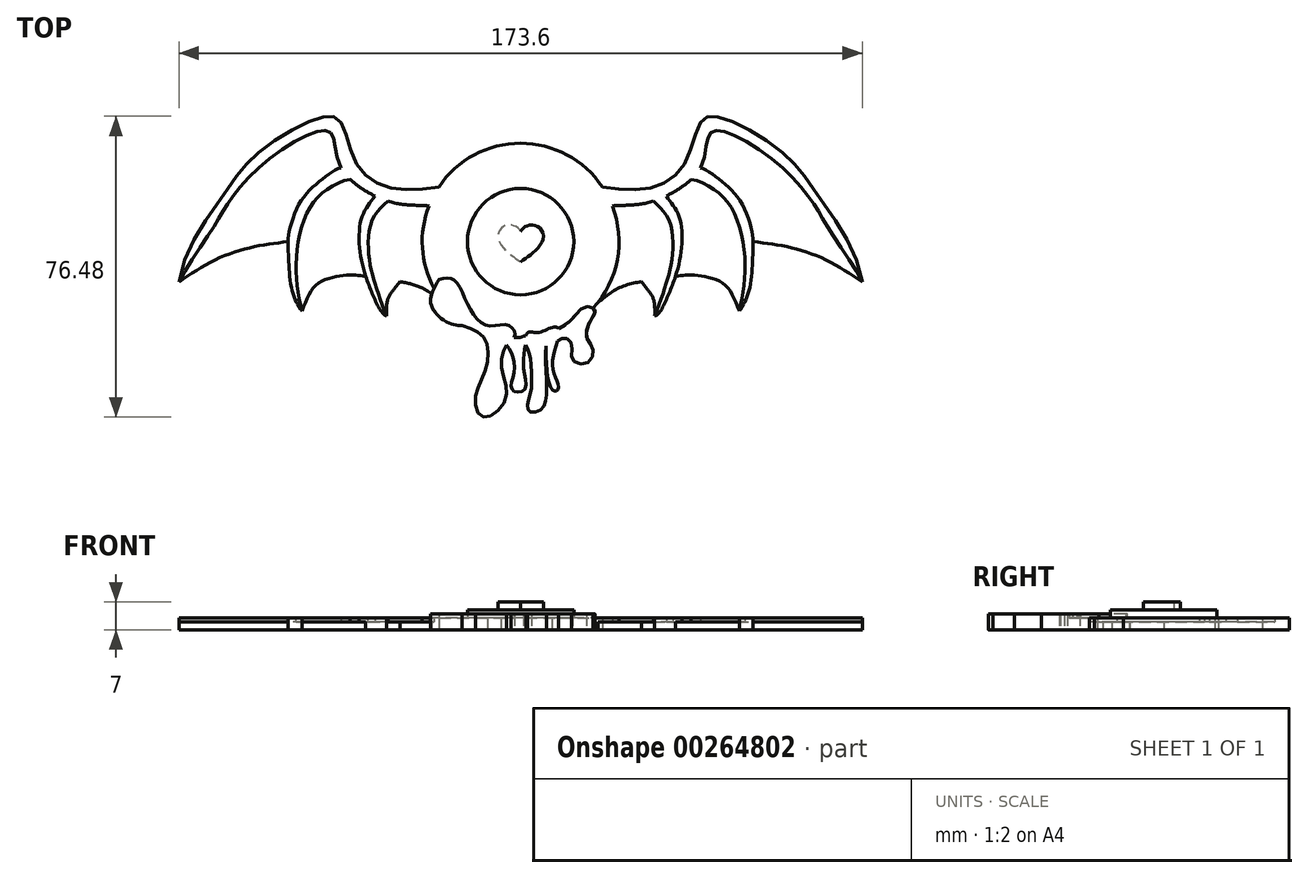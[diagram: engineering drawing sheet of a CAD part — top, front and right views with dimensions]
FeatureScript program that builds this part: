
annotation { "Feature Type Name" : "Feature", "Feature Type Description" : "" }
export const myFeature = defineFeature(function(context is Context, id is Id, definition is map)
    precondition{}
    {
        {
            var Q0;
            Q0=qCreatedBy(makeId("Top.planeOp"),FACE);
            var sketch = newSketch(context, id + "F0", { "sketchPlane" : qUnion([Q0])});
            skCircle(sketch, "E0", {"center": v(0, 0) * mm, "radius": 25 * mm});
            skLineSegment(sketch, "E1", {"start": v(0, 25) * mm, "end": v(0, -25) * mm, "construction": true});
            skFitSpline(sketch, "E2", {"points": [v(20.76, 13.92) * mm, v(34.08, 13.92) * mm, v(42, 20.48) * mm, v(46, 30.69) * mm, v(50.93, 31.48) * mm, v(67.03, 22.24) * mm, v(75.74, 11.46) * mm, v(86.8, -10.28) * mm], "startDerivative": vector(95.75, -17.53) * mm, "endDerivative": vector(18.54, -135.11) * mm});
            skFitSpline(sketch, "E3", {"points": [v(20.7, -14) * mm, v(37, -10.54) * mm, v(45, -8.07) * mm, v(66.66, 1.74) * mm, v(75.74, 11.46) * mm], "startDerivative": vector(59.46, -0.59) * mm, "endDerivative": vector(18.77, 28.66) * mm, "construction": true});
            skFitSpline(sketch, "E4", {"points": [v(23.3, 9.08) * mm, v(33.72, 10.28) * mm, v(45.64, 18.76) * mm, v(47.9, 27.18) * mm, v(51.1, 28.14) * mm, v(65.44, 19.69) * mm, v(74.45, 9.58) * mm, v(78.2, 3.43) * mm, v(86.8, -10.28) * mm], "startDerivative": vector(110.38, 5.87) * mm, "endDerivative": vector(40.39, -81.17) * mm});
            skFitSpline(sketch, "E5", {"points": [v(33.72, 10.28) * mm, v(37.86, 5.02) * mm, v(38.5, -3.9) * mm, v(37, -10.54) * mm, v(34.08, -18.9) * mm], "startDerivative": vector(21.3, -19.5) * mm, "endDerivative": vector(-13.55, -34.2) * mm});
            skFitSpline(sketch, "E6", {"points": [v(37, 11.6) * mm, v(40.25, 6.46) * mm, v(40.52, -4.24) * mm, v(37.2, -14.33) * mm, v(34.08, -18.9) * mm], "startDerivative": vector(14.85, -22) * mm, "endDerivative": vector(-16.96, -5.17) * mm});
            skFitSpline(sketch, "E7", {"points": [v(32.11, -12.01) * mm, v(33.72, -14.49) * mm, v(34.08, -18.9) * mm], "startDerivative": vector(4.43, -5.79) * mm, "endDerivative": vector(-0.15, -8.8) * mm});
            skFitSpline(sketch, "E8", {"points": [v(45.64, 18.76) * mm, v(50.26, 15.97) * mm, v(55.72, 10.44) * mm, v(58.9, 2) * mm, v(59.02, -2.64) * mm, v(58.1, -12.2) * mm, v(55.56, -17.62) * mm], "startDerivative": vector(28.21, -5.42) * mm, "endDerivative": vector(-19.1, -30.2) * mm});
            skFitSpline(sketch, "E9", {"points": [v(43.34, 15.84) * mm, v(49.55, 13.02) * mm, v(53.96, 7.9) * mm, v(56.67, -1.36) * mm, v(56.83, -10.28) * mm, v(55.56, -17.62) * mm], "startDerivative": vector(32.47, -4.35) * mm, "endDerivative": vector(-7.91, -36.84) * mm});
            skFitSpline(sketch, "E10", {"points": [v(38.97, -9.94) * mm, v(46.63, -10.28) * mm, v(52.84, -13.22) * mm, v(55.56, -17.62) * mm], "startDerivative": vector(21.38, 0.7) * mm, "endDerivative": vector(7.12, -15.9) * mm, "construction": true});
            skFitSpline(sketch, "E11", {"points": [v(59.1, 0) * mm, v(68, -1.36) * mm, v(77.72, -4.7) * mm, v(86.8, -10.28) * mm], "startDerivative": vector(27.78, -3.23) * mm, "endDerivative": vector(25.67, -17.5) * mm});
            skFitSpline(sketch, "E12", {"points": [v(19.62, -15.5) * mm, v(25.1, -11.72) * mm, v(30.69, -10.12) * mm], "startDerivative": vector(10.4, 8.3) * mm, "endDerivative": vector(11.78, 2.35) * mm});
            skFitSpline(sketch, "E13", {"points": [v(32.11, -12.01) * mm, v(30.69, -10.12) * mm], "startDerivative": vector(-1.42, 1.9) * mm, "endDerivative": vector(-1.42, 1.9) * mm});
            skFitSpline(sketch, "E14", {"points": [v(55.56, -17.62) * mm, v(52.05, -11.08) * mm, v(46.6, -8.83) * mm, v(42.13, -8.5) * mm, v(39.36, -8.79) * mm], "startDerivative": vector(-10.96, 25.87) * mm, "endDerivative": vector(-14.04, -2.02) * mm});
            skFitSpline(sketch, "E15", {"points": [v(20.76, 13.92) * mm, v(16.18, 9.49) * mm, v(19.62, -15.5) * mm], "startDerivative": vector(-16.85, -9.2) * mm, "endDerivative": vector(11.44, -45.62) * mm});
            skFitSpline(sketch, "E16.MirrorCS", {"points": [v(-20.76, 13.92) * mm, v(-16.18, 9.49) * mm, v(-19.62, -15.5) * mm], "startDerivative": vector(16.85, -9.2) * mm, "endDerivative": vector(-11.44, -45.62) * mm});
            skFitSpline(sketch, "E17.MirrorCS", {"points": [v(-23.3, 9.08) * mm, v(-33.72, 10.28) * mm, v(-45.64, 18.76) * mm, v(-47.9, 27.18) * mm, v(-51.1, 28.14) * mm, v(-65.44, 19.69) * mm, v(-74.45, 9.58) * mm, v(-78.2, 3.43) * mm, v(-86.8, -10.28) * mm], "startDerivative": vector(-110.38, 5.87) * mm, "endDerivative": vector(-40.39, -81.17) * mm});
            skFitSpline(sketch, "E18.MirrorCS", {"points": [v(-20.76, 13.92) * mm, v(-34.08, 13.92) * mm, v(-42, 20.48) * mm, v(-46, 30.69) * mm, v(-50.93, 31.48) * mm, v(-67.03, 22.24) * mm, v(-75.74, 11.46) * mm, v(-86.8, -10.28) * mm], "startDerivative": vector(-95.75, -17.53) * mm, "endDerivative": vector(-18.54, -135.11) * mm});
            skFitSpline(sketch, "E19.MirrorCS", {"points": [v(-33.72, 10.28) * mm, v(-37.86, 5.02) * mm, v(-38.5, -3.9) * mm, v(-37, -10.54) * mm, v(-34.08, -18.9) * mm], "startDerivative": vector(-21.3, -19.5) * mm, "endDerivative": vector(13.55, -34.2) * mm});
            skFitSpline(sketch, "E20.MirrorCS", {"points": [v(-37, 11.6) * mm, v(-40.25, 6.46) * mm, v(-40.52, -4.24) * mm, v(-37.2, -14.33) * mm, v(-34.08, -18.9) * mm], "startDerivative": vector(-14.85, -22) * mm, "endDerivative": vector(16.96, -5.17) * mm});
            skFitSpline(sketch, "E21.MirrorCS", {"points": [v(-43.34, 15.84) * mm, v(-49.55, 13.02) * mm, v(-53.96, 7.9) * mm, v(-56.67, -1.36) * mm, v(-56.83, -10.28) * mm, v(-55.56, -17.62) * mm], "startDerivative": vector(-32.47, -4.35) * mm, "endDerivative": vector(7.91, -36.84) * mm});
            skFitSpline(sketch, "E22.MirrorCS", {"points": [v(-45.64, 18.76) * mm, v(-50.26, 15.97) * mm, v(-55.72, 10.44) * mm, v(-58.9, 2) * mm, v(-59.02, -2.64) * mm, v(-58.1, -12.2) * mm, v(-55.56, -17.62) * mm], "startDerivative": vector(-28.21, -5.42) * mm, "endDerivative": vector(19.1, -30.2) * mm});
            skFitSpline(sketch, "E23.MirrorCS", {"points": [v(-19.62, -15.5) * mm, v(-25.1, -11.72) * mm, v(-30.69, -10.12) * mm], "startDerivative": vector(-10.4, 8.3) * mm, "endDerivative": vector(-11.78, 2.35) * mm});
            skFitSpline(sketch, "E24.MirrorCS", {"points": [v(-32.11, -12.01) * mm, v(-30.69, -10.12) * mm], "startDerivative": vector(1.42, 1.9) * mm, "endDerivative": vector(1.42, 1.9) * mm});
            skFitSpline(sketch, "E25.MirrorCS", {"points": [v(-32.11, -12.01) * mm, v(-33.72, -14.49) * mm, v(-34.08, -18.9) * mm], "startDerivative": vector(-4.43, -5.79) * mm, "endDerivative": vector(0.15, -8.8) * mm});
            skFitSpline(sketch, "E26.MirrorCS", {"points": [v(-59.1, 0) * mm, v(-68, -1.36) * mm, v(-77.72, -4.7) * mm, v(-86.8, -10.28) * mm], "startDerivative": vector(-27.78, -3.23) * mm, "endDerivative": vector(-25.67, -17.5) * mm});
            skFitSpline(sketch, "E27.MirrorCS", {"points": [v(-55.56, -17.62) * mm, v(-52.05, -11.08) * mm, v(-46.6, -8.83) * mm, v(-42.13, -8.5) * mm, v(-39.36, -8.79) * mm], "startDerivative": vector(10.96, 25.87) * mm, "endDerivative": vector(14.04, -2.02) * mm});
            skSolve(sketch);
        }
        {
            var Q0;
            {var subQ0=sQuery(id+"F0.wireOp",EDGE,"E15");Q0=makeQuery(id+"F0.imprint","IMPRINT",FACE,{"disambiguationData":[TD([[makeQuery(id+"F0.imprint","IMPRINT",EDGE,{"derivedFrom":subQ0}),-1.0]])]});}
            var Q1;
            {var subQ0=sQuery(id+"F0.wireOp",EDGE,"E15");Q1=makeQuery(id+"F0.imprint","IMPRINT",FACE,{"disambiguationData":[TD([[makeQuery(id+"F0.imprint","IMPRINT",EDGE,{"derivedFrom":subQ0}),1.0]])]});}
            var Q2;
            {var subQ0=sQuery(id+"F0.wireOp",EDGE,"E16.MirrorCS");Q2=makeQuery(id+"F0.imprint","IMPRINT",FACE,{"disambiguationData":[TD([[makeQuery(id+"F0.imprint","IMPRINT",EDGE,{"derivedFrom":subQ0}),-1.0]])]});}
            extrude(context, id + "F1", {"entities" : qUnion([Q0, Q1, Q2]), "depth" : 3 * mm, "offsetDistance" : 25 * mm});
        }
        {
            var Q0;
            Q0=qCreatedBy(makeId("Top.planeOp"),FACE);
            var sketch = newSketch(context, id + "F2", { "sketchPlane" : qUnion([Q0])});
            skCircle(sketch, "E28", {"center": v(0, 0) * mm, "radius": 13.5 * mm});
            skSolve(sketch);
        }
        {
            var Q0;
            Q0=qSketchRegion(id+"F2",true);
            extrude(context, id + "F3", {"entities" : qUnion([Q0]), "operationType" : NewBodyOperationType.ADD, "depth" : 5 * mm, "offsetDistance" : 25 * mm});
        }
        {
            var Q0;
            {var subQ4=sQuery(id+"F0.wireOp",EDGE,"E2");Q0=makeQuery(id+"F0.imprint","IMPRINT",FACE,{"disambiguationData":[TD([[makeQuery(id+"F0.imprint","IMPRINT",EDGE,{"derivedFrom":subQ4}),-1.0]])]});}
            var Q1;
            {var subQ0=sQuery(id+"F0.wireOp",EDGE,"E15");Q1=makeQuery(id+"F0.imprint","IMPRINT",FACE,{"disambiguationData":[TD([[makeQuery(id+"F0.imprint","IMPRINT",EDGE,{"derivedFrom":subQ0}),1.0]])]});}
            var Q2;
            {var subQ0=sQuery(id+"F0.wireOp",EDGE,"E5");Q2=makeQuery(id+"F0.imprint","IMPRINT",FACE,{"disambiguationData":[TD([[makeQuery(id+"F0.imprint","IMPRINT",EDGE,{"derivedFrom":subQ0}),-1.0]])]});}
            var Q3;
            {var subQ0=sQuery(id+"F0.wireOp",EDGE,"E5");Q3=makeQuery(id+"F0.imprint","IMPRINT",FACE,{"disambiguationData":[TD([[makeQuery(id+"F0.imprint","IMPRINT",EDGE,{"derivedFrom":subQ0}),1.0]])]});}
            var Q4;
            {var subQ3=sQuery(id+"F0.wireOp",EDGE,"E9");Q4=makeQuery(id+"F0.imprint","IMPRINT",FACE,{"disambiguationData":[TD([[makeQuery(id+"F0.imprint","IMPRINT",EDGE,{"derivedFrom":subQ3}),-1.0]])]});}
            var Q5;
            {var subQ3=sQuery(id+"F0.wireOp",EDGE,"E9");Q5=makeQuery(id+"F0.imprint","IMPRINT",FACE,{"disambiguationData":[TD([[makeQuery(id+"F0.imprint","IMPRINT",EDGE,{"derivedFrom":subQ3}),1.0]])]});}
            var Q6;
            {var subQ0=sQuery(id+"F0.wireOp",EDGE,"E11");Q6=makeQuery(id+"F0.imprint","IMPRINT",FACE,{"disambiguationData":[TD([[makeQuery(id+"F0.imprint","IMPRINT",EDGE,{"derivedFrom":subQ0}),1.0]])]});}
            var Q7;
            {var subQ1=sQuery(id+"F0.wireOp",EDGE,"E19.MirrorCS");Q7=makeQuery(id+"F0.imprint","IMPRINT",FACE,{"disambiguationData":[TD([[makeQuery(id+"F0.imprint","IMPRINT",EDGE,{"derivedFrom":subQ1}),1.0]])]});}
            var Q8;
            {var subQ3=sQuery(id+"F0.wireOp",EDGE,"E21.MirrorCS");Q8=makeQuery(id+"F0.imprint","IMPRINT",FACE,{"disambiguationData":[TD([[makeQuery(id+"F0.imprint","IMPRINT",EDGE,{"derivedFrom":subQ3}),1.0]])]});}
            var Q9;
            {var subQ0=sQuery(id+"F0.wireOp",EDGE,"E19.MirrorCS");Q9=makeQuery(id+"F0.imprint","IMPRINT",FACE,{"disambiguationData":[TD([[makeQuery(id+"F0.imprint","IMPRINT",EDGE,{"derivedFrom":subQ0}),-1.0]])]});}
            var Q10;
            {var subQ6=sQuery(id+"F0.wireOp",EDGE,"E18.MirrorCS");Q10=makeQuery(id+"F0.imprint","IMPRINT",FACE,{"disambiguationData":[TD([[makeQuery(id+"F0.imprint","IMPRINT",EDGE,{"derivedFrom":subQ6}),1.0]])]});}
            var Q11;
            {var subQ0=sQuery(id+"F0.wireOp",EDGE,"E26.MirrorCS");Q11=makeQuery(id+"F0.imprint","IMPRINT",FACE,{"disambiguationData":[TD([[makeQuery(id+"F0.imprint","IMPRINT",EDGE,{"derivedFrom":subQ0}),-1.0]])]});}
            var Q12;
            {var subQ0=sQuery(id+"F0.wireOp",EDGE,"E21.MirrorCS");Q12=makeQuery(id+"F0.imprint","IMPRINT",FACE,{"disambiguationData":[TD([[makeQuery(id+"F0.imprint","IMPRINT",EDGE,{"derivedFrom":subQ0}),-1.0]])]});}
            var Q13;
            {var subQ0=sQuery(id+"F0.wireOp",EDGE,"E16.MirrorCS");Q13=makeQuery(id+"F0.imprint","IMPRINT",FACE,{"disambiguationData":[TD([[makeQuery(id+"F0.imprint","IMPRINT",EDGE,{"derivedFrom":subQ0}),-1.0]])]});}
            extrude(context, id + "F4", {"entities" : qUnion([Q0, Q1, Q2, Q3, Q4, Q5, Q6, Q7, Q8, Q9, Q10, Q11, Q12, Q13]), "operationType" : NewBodyOperationType.ADD, "depth" : 2 * mm, "offsetDistance" : 25 * mm});
        }
        {
            var Q0;
            {var subQ4=sQuery(id+"F0.wireOp",EDGE,"E2");Q0=makeQuery(id+"F0.imprint","IMPRINT",FACE,{"disambiguationData":[TD([[makeQuery(id+"F0.imprint","IMPRINT",EDGE,{"derivedFrom":subQ4}),-1.0]])]});}
            var Q1;
            {var subQ0=sQuery(id+"F0.wireOp",EDGE,"E5");Q1=makeQuery(id+"F0.imprint","IMPRINT",FACE,{"disambiguationData":[TD([[makeQuery(id+"F0.imprint","IMPRINT",EDGE,{"derivedFrom":subQ0}),1.0]])]});}
            var Q2;
            {var subQ3=sQuery(id+"F0.wireOp",EDGE,"E9");Q2=makeQuery(id+"F0.imprint","IMPRINT",FACE,{"disambiguationData":[TD([[makeQuery(id+"F0.imprint","IMPRINT",EDGE,{"derivedFrom":subQ3}),1.0]])]});}
            var Q3;
            {var subQ6=sQuery(id+"F0.wireOp",EDGE,"E18.MirrorCS");Q3=makeQuery(id+"F0.imprint","IMPRINT",FACE,{"disambiguationData":[TD([[makeQuery(id+"F0.imprint","IMPRINT",EDGE,{"derivedFrom":subQ6}),1.0]])]});}
            var Q4;
            {var subQ0=sQuery(id+"F0.wireOp",EDGE,"E19.MirrorCS");Q4=makeQuery(id+"F0.imprint","IMPRINT",FACE,{"disambiguationData":[TD([[makeQuery(id+"F0.imprint","IMPRINT",EDGE,{"derivedFrom":subQ0}),-1.0]])]});}
            var Q5;
            {var subQ0=sQuery(id+"F0.wireOp",EDGE,"E21.MirrorCS");Q5=makeQuery(id+"F0.imprint","IMPRINT",FACE,{"disambiguationData":[TD([[makeQuery(id+"F0.imprint","IMPRINT",EDGE,{"derivedFrom":subQ0}),-1.0]])]});}
            extrude(context, id + "F5", {"entities" : qUnion([Q0, Q1, Q2, Q3, Q4, Q5]), "operationType" : NewBodyOperationType.ADD, "depth" : 3 * mm, "offsetDistance" : 25 * mm});
        }
        {
            var Q0;
            Q0=qCreatedBy(makeId("Top.planeOp"),FACE);
            var sketch = newSketch(context, id + "F6", { "sketchPlane" : qUnion([Q0])});
            skFitSpline(sketch, "E29", {"points": [v(-20.72, -9.64) * mm, v(-22.8, -15.86) * mm, v(-18.33, -20.64) * mm, v(-14.83, -21.28) * mm], "startDerivative": vector(-10.43, -17.24) * mm, "endDerivative": vector(12.17, -0.13) * mm});
            skFitSpline(sketch, "E30", {"points": [v(-20.72, -9.64) * mm, v(-17.06, -9.64) * mm, v(-13.55, -15.7) * mm, v(-8.6, -21.28) * mm, v(-3.03, -21.28) * mm, v(-1.44, -23.83) * mm, v(-3.5, -26.22) * mm, v(-4.78, -32.28) * mm, v(-3.83, -40.1) * mm, v(-9.4, -44.56) * mm, v(-11.48, -39.61) * mm, v(-8.77, -31.96) * mm, v(-9.25, -24.47) * mm, v(-14.83, -21.28) * mm], "startDerivative": vector(65.16, 15.52) * mm, "endDerivative": vector(-82.7, 27.37) * mm});
            skFitSpline(sketch, "E31", {"points": [v(-3.5, -26.22) * mm, v(-1.91, -29.41) * mm, v(-1.75, -33.72) * mm, v(-2.4, -36.9) * mm, v(-1.4, -38.14) * mm, v(1.08, -37.54) * mm, v(0.92, -33.52) * mm, v(0.76, -29.33) * mm, v(1.27, -25.74) * mm, v(1.2, -23.95) * mm, v(0, -24.31) * mm, v(-1.64, -24.31) * mm], "startDerivative": vector(18.13, -28.93) * mm, "endDerivative": vector(-23.4, 3.66) * mm});
            skFitSpline(sketch, "E32", {"points": [v(1.2, -23.95) * mm, v(2.14, -22.96) * mm, v(4.4, -23.08) * mm, v(7.95, -21.84) * mm, v(9.81, -22.12) * mm, v(8.9, -26.63) * mm, v(8.29, -32.94) * mm, v(9.64, -36.71) * mm, v(8.96, -37.95) * mm, v(7.5, -36.77) * mm, v(6.41, -26.5) * mm], "startDerivative": vector(11.67, 19.38) * mm, "endDerivative": vector(-1.14, 43.55) * mm});
            skFitSpline(sketch, "E33", {"points": [v(1.2, -26.22) * mm, v(2.1, -28.1) * mm, v(2.77, -32.66) * mm, v(2.49, -38.68) * mm, v(1.73, -41.67) * mm, v(2.36, -43.24) * mm, v(5.02, -42.75) * mm, v(6.41, -40.17) * mm, v(6.5, -34.48) * mm, v(6.41, -26.5) * mm], "startDerivative": vector(11, -19.03) * mm, "endDerivative": vector(3.74, 33.89) * mm});
            skFitSpline(sketch, "E34", {"points": [v(9.81, -22.12) * mm, v(13.2, -19.51) * mm, v(16.5, -16.57) * mm, v(18.88, -17.43) * mm, v(17.55, -20.46) * mm, v(16.89, -24.53) * mm, v(18.4, -27.47) * mm, v(16.89, -30.8) * mm, v(13.2, -29.94) * mm, v(13.1, -26.43) * mm, v(11.39, -24.53) * mm, v(9.34, -25.28) * mm], "startDerivative": vector(34.2, 22.05) * mm, "endDerivative": vector(-27.8, -17.8) * mm});
            skSolve(sketch);
        }
        {
            var Q0;
            {var subQ0=sQuery(id+"F6.wireOp",EDGE,"E29");Q0=makeQuery(id+"F6.imprint","IMPRINT",FACE,{"disambiguationData":[TD([[makeQuery(id+"F6.imprint","IMPRINT",EDGE,{"derivedFrom":subQ0}),1.0]])]});}
            var Q1;
            {var subQ0=sQuery(id+"F6.wireOp",EDGE,"E31");var subQ1=sQuery(id+"F6.wireOp",EDGE,"E30");var subQ2=makeQuery(id+"F6.imprint","INTERSECT",VERTEX,{"disambiguationData":[OD(0.0)],"derivedFrom":[subQ1,subQ0]});Q1=makeQuery(id+"F6.imprint","IMPRINT",FACE,{"disambiguationData":[TD([[makeQuery(id+"F6.imprint","IMPRINT",EDGE,{"disambiguationData":[TD([[subQ2,1.0]])],"derivedFrom":subQ1}),1.0]])]});}
            var Q2;
            {var subQ0=sQuery(id+"F6.wireOp",EDGE,"E33");Q2=makeQuery(id+"F6.imprint","IMPRINT",FACE,{"disambiguationData":[TD([[makeQuery(id+"F6.imprint","IMPRINT",EDGE,{"derivedFrom":subQ0}),1.0]])]});}
            var Q3;
            {var subQ0=sQuery(id+"F6.wireOp",EDGE,"E34");Q3=makeQuery(id+"F6.imprint","IMPRINT",FACE,{"disambiguationData":[TD([[makeQuery(id+"F6.imprint","IMPRINT",EDGE,{"derivedFrom":subQ0}),-1.0]])]});}
            extrude(context, id + "F7", {"entities" : qUnion([Q0, Q1, Q2, Q3]), "operationType" : NewBodyOperationType.ADD, "depth" : 4 * mm, "offsetDistance" : 25 * mm});
        }
        {
            var Q0;
            Q0=makeQuery(id+"F3.opExtrude","CAP_FACE",FACE,{"disambiguationData":[OSD([sQuery(id+"F2.wireOp",EDGE,"E28")])],"isStart":false});
            var sketch = newSketch(context, id + "F8", { "sketchPlane" : qUnion([Q0])});
            skFitSpline(sketch, "E35", {"points": [v(0, 2.56) * mm, v(-1.46, 3.94) * mm, v(-4.21, 3.94) * mm, v(-5.75, 0.99) * mm, v(-3.12, -2.8) * mm, v(0, -5.13) * mm], "startDerivative": vector(-7.08, 12.17) * mm, "endDerivative": vector(14.96, -10.49) * mm});
            skFitSpline(sketch, "E36.MirrorCS", {"points": [v(0, 2.56) * mm, v(1.46, 3.94) * mm, v(4.21, 3.94) * mm, v(5.75, 0.99) * mm, v(3.12, -2.8) * mm, v(0, -5.13) * mm], "startDerivative": vector(7.08, 12.17) * mm, "endDerivative": vector(-14.96, -10.49) * mm});
            skSolve(sketch);
        }
        {
            var Q0;
            Q0=makeQuery(id+"F8.imprint","IMPRINT",FACE,{"disambiguationData":[TD([[makeQuery(id+"F8.imprint","IMPRINT",EDGE,{"derivedFrom":sQuery(id+"F8.wireOp",EDGE,"E35")}),1.0]])]});
            extrude(context, id + "F9", {"entities" : qUnion([Q0]), "operationType" : NewBodyOperationType.ADD, "depth" : 2 * mm, "offsetDistance" : 25 * mm});
        }
    });
